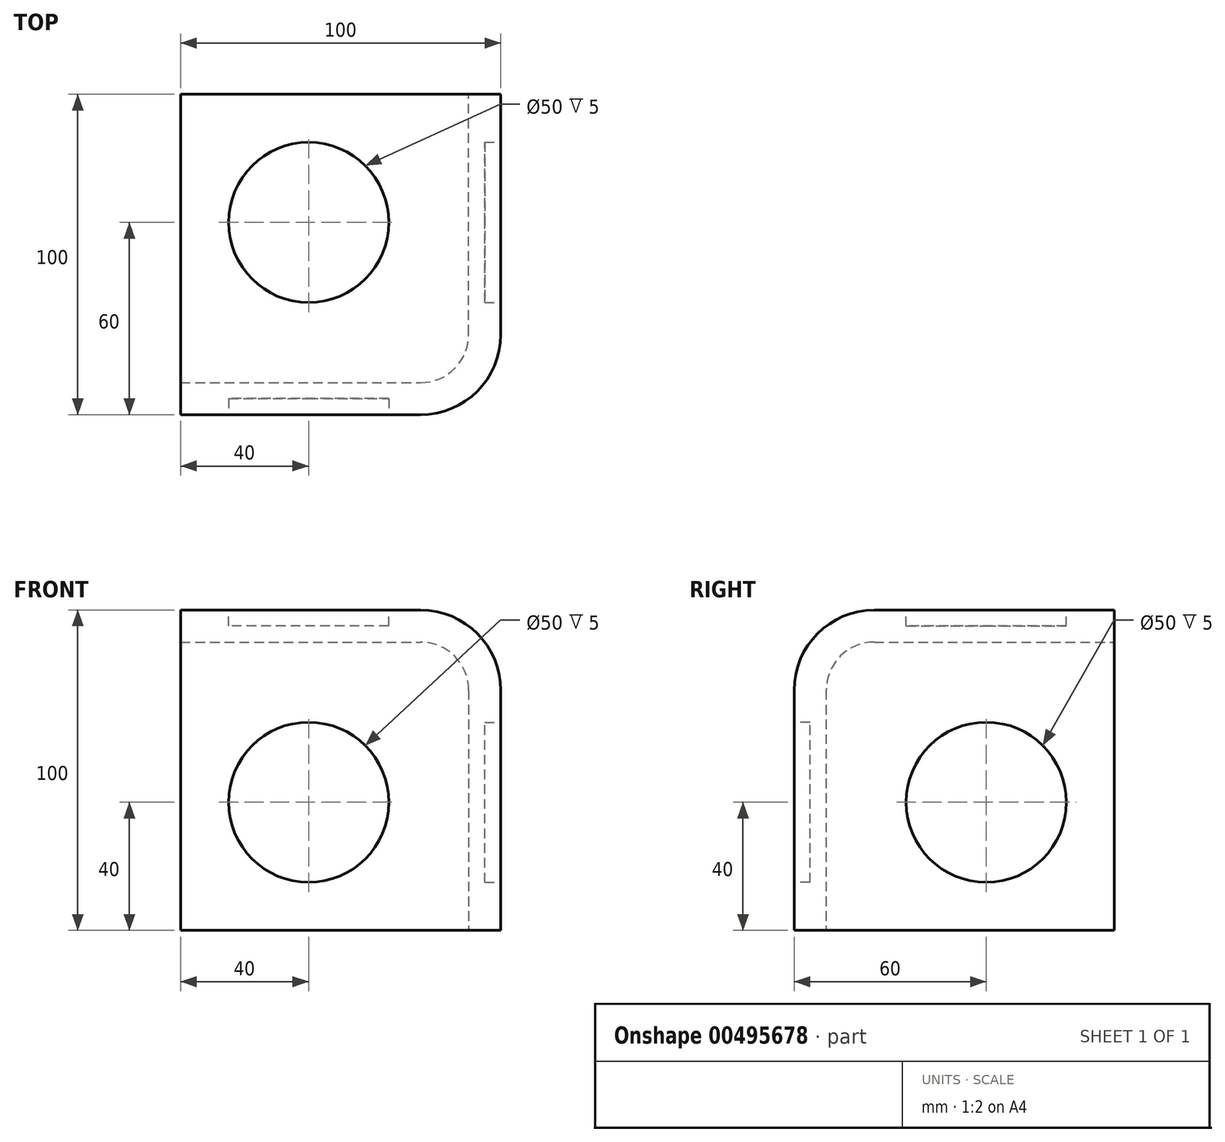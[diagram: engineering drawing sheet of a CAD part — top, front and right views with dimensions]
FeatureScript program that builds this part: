
annotation { "Feature Type Name" : "Feature", "Feature Type Description" : "" }
export const myFeature = defineFeature(function(context is Context, id is Id, definition is map)
    precondition{}
    {
        {
            var Q0;
            Q0=qCreatedBy(makeId("Front.planeOp"),FACE);
            var sketch = newSketch(context, id + "F0", { "sketchPlane" : qUnion([Q0])});
            skLineSegment(sketch, "E0.bottom", {"start": v(-50, 50) * mm, "end": v(50, 50) * mm});
            skLineSegment(sketch, "E0.top", {"start": v(-50, -50) * mm, "end": v(50, -50) * mm});
            skLineSegment(sketch, "E0.left", {"start": v(-50, 50) * mm, "end": v(-50, -50) * mm});
            skLineSegment(sketch, "E0.right", {"start": v(50, 50) * mm, "end": v(50, -50) * mm});
            skSolve(sketch);
        }
        {
            var Q0;
            Q0 = qSketchRegion(id + "F0", true);
            extrude(context, id + "F1", {"entities" : qUnion([Q0]), "depth" : 100 * mm});
        }
        {
            var Q0;
            Q0=makeQuery(id+"F1.opExtrude","CAP_EDGE",EDGE,{"disambiguationData":[OSD([sQuery(id+"F0.wireOp",EDGE,"E0.bottom")])],"isStart":false});
            var Q1;
            Q1=makeQuery(id+"F1.opExtrude","SWEPT_EDGE",EDGE,{"disambiguationData":[OSD([sQuery(id+"F0.wireOp",EDGE,"E0.bottom"),sQuery(id+"F0.wireOp",EDGE,"E0.right")])]});
            var Q2;
            Q2=makeQuery(id+"F1.opExtrude","CAP_EDGE",EDGE,{"disambiguationData":[OSD([sQuery(id+"F0.wireOp",EDGE,"E0.right")])],"isStart":false});
            fillet(context, id + "F2", {"entities" : qUnion([Q0, Q1, Q2]), "radius" : 25 * mm, "tangentPropagation" : true, "allowEdgeOverflow" : false});
        }
        {
            var Q0;
            Q0=makeQuery(id+"F1.opExtrude","SWEPT_FACE",FACE,{"disambiguationData":[OSD([sQuery(id+"F0.wireOp",EDGE,"E0.left")])]});
            var Q1;
            Q1=makeQuery(id+"F1.opExtrude","CAP_FACE",FACE,{"disambiguationData":[OSD([sQuery(id+"F0.wireOp",EDGE,"E0.bottom"),sQuery(id+"F0.wireOp",EDGE,"E0.top"),sQuery(id+"F0.wireOp",EDGE,"E0.left"),sQuery(id+"F0.wireOp",EDGE,"E0.right")])],"isStart":true});
            var Q2;
            Q2=makeQuery(id+"F1.opExtrude","SWEPT_FACE",FACE,{"disambiguationData":[OSD([sQuery(id+"F0.wireOp",EDGE,"E0.top")])]});
            shell(context, id + "F3", {"entities" : qUnion([Q0, Q1, Q2]), "thickness" : 10 * mm});
        }
        {
            var Q0;
            Q0=makeQuery(id+"F1.opExtrude","CAP_FACE",FACE,{"disambiguationData":[OSD([sQuery(id+"F0.wireOp",EDGE,"E0.bottom"),sQuery(id+"F0.wireOp",EDGE,"E0.top"),sQuery(id+"F0.wireOp",EDGE,"E0.left"),sQuery(id+"F0.wireOp",EDGE,"E0.right")])],"isStart":false});
            var sketch = newSketch(context, id + "F4", { "sketchPlane" : qUnion([Q0])});
            skCircle(sketch, "E1", {"center": v(-10, -10) * mm, "radius": 25 * mm});
            skSolve(sketch);
        }
        {
            var Q0;
            Q0=makeQuery(id+"F4.imprint","IMPRINT",FACE,{"disambiguationData":[TD([[makeQuery(id+"F4.imprint","IMPRINT",EDGE,{"derivedFrom":sQuery(id+"F4.wireOp",EDGE,"E1")}),1.0]])]});
            extrude(context, id + "F5", {"entities" : qUnion([Q0]), "operationType" : NewBodyOperationType.REMOVE, "oppositeDirection" : true, "depth" : 5 * mm});
        }
        {
            var Q0;
            Q0=makeQuery(id+"F1.opExtrude","SWEPT_FACE",FACE,{"disambiguationData":[OSD([sQuery(id+"F0.wireOp",EDGE,"E0.right")])]});
            var sketch = newSketch(context, id + "F6", { "sketchPlane" : qUnion([Q0])});
            skCircle(sketch, "E2", {"center": v(-40, -10) * mm, "radius": 25 * mm});
            skSolve(sketch);
        }
        {
            var Q0;
            Q0 = qSketchRegion(id + "F6", true);
            extrude(context, id + "F7", {"entities" : qUnion([Q0]), "operationType" : NewBodyOperationType.REMOVE, "oppositeDirection" : true, "depth" : 5 * mm});
        }
        {
            var Q0;
            Q0=makeQuery(id+"F1.opExtrude","SWEPT_FACE",FACE,{"disambiguationData":[OSD([sQuery(id+"F0.wireOp",EDGE,"E0.bottom")])]});
            var sketch = newSketch(context, id + "F8", { "sketchPlane" : qUnion([Q0])});
            skCircle(sketch, "E3", {"center": v(-10, -40) * mm, "radius": 25 * mm});
            skSolve(sketch);
        }
        {
            var Q0;
            Q0 = qSketchRegion(id + "F8", true);
            extrude(context, id + "F9", {"entities" : qUnion([Q0]), "operationType" : NewBodyOperationType.REMOVE, "oppositeDirection" : true, "depth" : 5 * mm});
        }
    });
